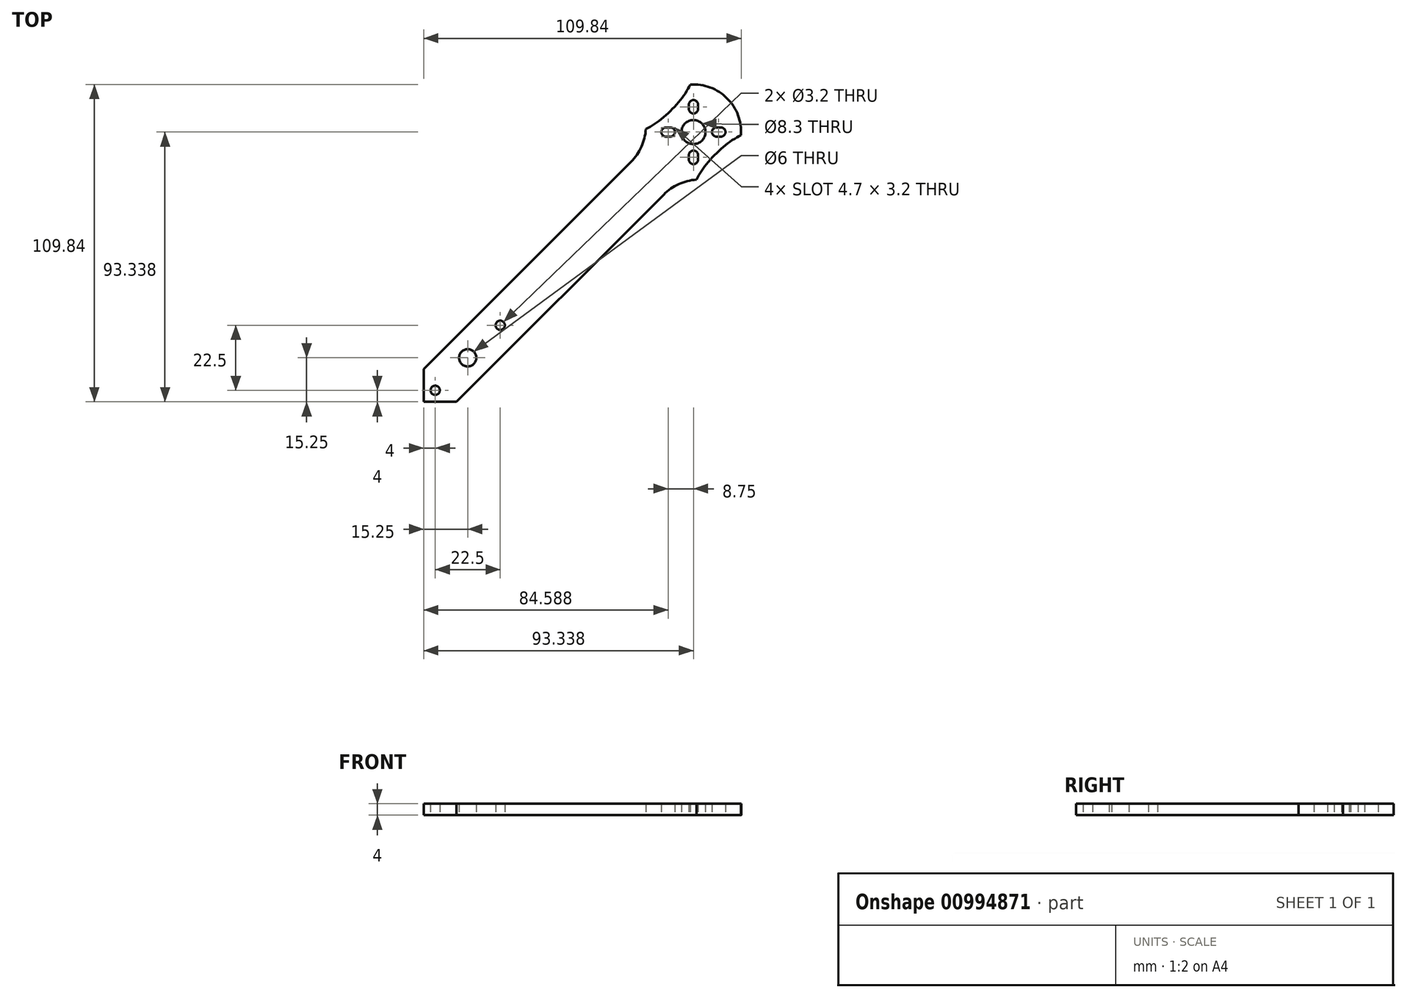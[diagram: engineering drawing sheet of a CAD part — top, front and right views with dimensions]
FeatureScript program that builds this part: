
annotation { "Feature Type Name" : "Feature", "Feature Type Description" : "" }
export const myFeature = defineFeature(function(context is Context, id is Id, definition is map)
    precondition{}
    {
        {
            var Q0;
            Q0=qCreatedBy(makeId("Top.planeOp"),FACE);
            var sketch = newSketch(context, id + "F0", { "sketchPlane" : qUnion([Q0])});
            skLineSegment(sketch, "E0.bottom", {"start": v(-18, 50) * mm, "end": v(18, 50) * mm, "construction": true});
            skLineSegment(sketch, "E0.top", {"start": v(-18, -50) * mm, "end": v(18, -50) * mm, "construction": true});
            skLineSegment(sketch, "E0.left", {"start": v(-18, 50) * mm, "end": v(-18, -50) * mm, "construction": true});
            skLineSegment(sketch, "E0.right", {"start": v(18, 50) * mm, "end": v(18, -50) * mm, "construction": true});
            skPoint(sketch, "E0.middle", {"position": v(0, 0) * mm});
            skLineSegment(sketch, "E1", {"start": v(0, 0) * mm, "end": v(15.25, 0) * mm, "construction": true});
            skLineSegment(sketch, "E2", {"start": v(15.25, 0) * mm, "end": v(15.25, 15.25) * mm, "construction": true});
            skCircle(sketch, "E3", {"center": v(15.25, 15.25) * mm, "radius": 3 * mm});
            skCircle(sketch, "E4.MirrorC", {"center": v(15.25, -15.25) * mm, "radius": 3 * mm, "construction": true});
            skCircle(sketch, "E5.MirrorC", {"center": v(-15.25, -15.25) * mm, "radius": 3 * mm, "construction": true});
            skCircle(sketch, "E6.MirrorC", {"center": v(-15.25, 15.25) * mm, "radius": 3 * mm, "construction": true});
            skLineSegment(sketch, "E7", {"start": v(0, 0) * mm, "end": v(93.34, 93.34) * mm, "construction": true});
            skLineSegment(sketch, "E8", {"start": v(93.34, 93.34) * mm, "end": v(87.68, 99) * mm});
            skLineSegment(sketch, "E9", {"start": v(87.68, 99) * mm, "end": v(99, 87.68) * mm});
            skLineSegment(sketch, "E10", {"start": v(99, 87.68) * mm, "end": v(11.31, 0) * mm});
            skLineSegment(sketch, "E11", {"start": v(11.31, 0) * mm, "end": v(0, 0) * mm});
            skLineSegment(sketch, "E12", {"start": v(87.68, 99) * mm, "end": v(0, 11.31) * mm});
            skLineSegment(sketch, "E13", {"start": v(0, 11.31) * mm, "end": v(0, 0) * mm});
            skCircle(sketch, "E14", {"center": v(93.34, 93.34) * mm, "radius": 16.5 * mm});
            skLineSegment(sketch, "E15", {"start": v(0, 0) * mm, "end": v(4, 0) * mm, "construction": true});
            skLineSegment(sketch, "E16", {"start": v(4, 0) * mm, "end": v(4, 4) * mm, "construction": true});
            skLineSegment(sketch, "E17", {"start": v(4, 4) * mm, "end": v(0, 4) * mm, "construction": true});
            skCircle(sketch, "E18", {"center": v(4, 4) * mm, "radius": 1.6 * mm});
            skLineSegment(sketch, "E19", {"start": v(93.34, 93.34) * mm, "end": v(100.06, 86.62) * mm, "construction": true});
            skCircle(sketch, "E20", {"center": v(100.06, 86.62) * mm, "radius": 1.6 * mm, "construction": true});
            skCircle(sketch, "E21", {"center": v(99, 87.68) * mm, "radius": 1.6 * mm, "construction": true});
            skLineSegment(sketch, "E22", {"start": v(101.19, 87.75) * mm, "end": v(100.13, 88.81) * mm, "construction": true});
            skLineSegment(sketch, "E23", {"start": v(98.93, 85.48) * mm, "end": v(97.86, 86.56) * mm, "construction": true});
            skLineSegment(sketch, "E24", {"start": v(93.34, 93.34) * mm, "end": v(97.6, 91.57) * mm, "construction": true});
            skLineSegment(sketch, "E25", {"start": v(93.34, 93.34) * mm, "end": v(93.34, 77.05) * mm, "construction": true});
            skCircle(sketch, "E26", {"center": v(93.34, 93.34) * mm, "radius": 4.15 * mm});
            skLineSegment(sketch, "E27.MirrorCS", {"start": v(102.84, 91.74) * mm, "end": v(101.34, 91.74) * mm});
            skCircle(sketch, "E28.MirrorC", {"center": v(101.34, 93.34) * mm, "radius": 1.6 * mm});
            skCircle(sketch, "E29.MirrorC", {"center": v(102.84, 93.34) * mm, "radius": 1.6 * mm});
            skLineSegment(sketch, "E30.MirrorCS", {"start": v(94.94, 83.84) * mm, "end": v(94.94, 85.34) * mm});
            skCircle(sketch, "E31.MirrorC", {"center": v(93.34, 83.84) * mm, "radius": 1.6 * mm});
            skCircle(sketch, "E32.MirrorC", {"center": v(93.34, 85.34) * mm, "radius": 1.6 * mm});
            skLineSegment(sketch, "E33.MirrorCS", {"start": v(91.74, 102.84) * mm, "end": v(91.74, 101.34) * mm});
            skCircle(sketch, "E34.MirrorC", {"center": v(93.34, 101.34) * mm, "radius": 1.6 * mm});
            skCircle(sketch, "E35.MirrorC", {"center": v(93.34, 102.84) * mm, "radius": 1.6 * mm});
            skCircle(sketch, "E36.MirrorC", {"center": v(85.34, 93.34) * mm, "radius": 1.6 * mm});
            skCircle(sketch, "E37.MirrorC", {"center": v(83.84, 93.34) * mm, "radius": 1.6 * mm});
            skLineSegment(sketch, "E38.MirrorCS", {"start": v(83.84, 94.94) * mm, "end": v(85.34, 94.94) * mm});
            skLineSegment(sketch, "E39", {"start": v(90.12, 93.34) * mm, "end": v(93.34, 93.34) * mm, "construction": true});
            skLineSegment(sketch, "E40", {"start": v(102.84, 93.34) * mm, "end": v(102.84, 94.94) * mm, "construction": true});
            skLineSegment(sketch, "E41", {"start": v(101.34, 93.34) * mm, "end": v(101.34, 94.94) * mm, "construction": true});
            skLineSegment(sketch, "E42", {"start": v(101.34, 94.94) * mm, "end": v(102.84, 94.94) * mm});
            skLineSegment(sketch, "E43.MirrorCS", {"start": v(93.34, 96.54) * mm, "end": v(100.06, 103.26) * mm, "construction": true});
            skLineSegment(sketch, "E44.MirrorCS", {"start": v(91.74, 85.34) * mm, "end": v(91.74, 83.84) * mm});
            skLineSegment(sketch, "E45.MirrorCS", {"start": v(85.34, 91.74) * mm, "end": v(83.84, 91.74) * mm});
            skLineSegment(sketch, "E46.MirrorCS", {"start": v(94.94, 101.34) * mm, "end": v(94.94, 102.84) * mm});
            skLineSegment(sketch, "E47", {"start": v(89.05, 97.63) * mm, "end": v(81.67, 105) * mm, "construction": true});
            skLineSegment(sketch, "E48", {"start": v(81.67, 105) * mm, "end": v(70.6, 93.93) * mm, "construction": true});
            skEllipse(sketch, "E49", {"center": v(81.67, 105) * mm, "majorRadius": 15.66 * mm, "minorRadius": 5.72 * mm, "majorAxis": v(-0.7, -0.7)});
            skEllipse(sketch, "E50.MirrorC", {"center": v(105, 81.67) * mm, "majorRadius": 15.66 * mm, "minorRadius": 5.72 * mm, "majorAxis": v(-0.7, -0.7)});
            skCircle(sketch, "E51", {"center": v(93.34, 93.34) * mm, "radius": 77.5 * mm, "construction": true});
            skCircle(sketch, "E52", {"center": v(26.5, 26.5) * mm, "radius": 1.6 * mm});
            skSolve(sketch);
        }
        {
            var Q0;
            Q0=makeQuery(id+"F0.imprint","IMPRINT",FACE,{"disambiguationData":[TD([[makeQuery(id+"F0.imprint","IMPRINT",EDGE,{"derivedFrom":sQuery(id+"F0.wireOp",EDGE,"E3")}),-1.0]])]});
            var Q1;
            {var subQ0=sQuery(id+"F0.wireOp",EDGE,"E30.MirrorCS");Q1=makeQuery(id+"F0.imprint","IMPRINT",FACE,{"disambiguationData":[TD([[makeQuery(id+"F0.imprint","IMPRINT",EDGE,{"derivedFrom":subQ0}),-1.0]])]});}
            var Q2;
            {var subQ18=sQuery(id+"F0.wireOp",EDGE,"E27.MirrorCS");Q2=makeQuery(id+"F0.imprint","IMPRINT",FACE,{"disambiguationData":[TD([[makeQuery(id+"F0.imprint","IMPRINT",EDGE,{"derivedFrom":subQ18}),1.0]])]});}
            extrude(context, id + "F1", {"entities" : qUnion([Q0, Q1, Q2]), "depth" : 4 * mm, "offsetDistance" : 25 * mm});
        }
        {
            var Q0;
            Q0=makeQuery(id+"F1.opExtrude","SWEPT_EDGE",EDGE,{"disambiguationData":[OSD([sQuery(id+"F0.wireOp",EDGE,"E10"),sQuery(id+"F0.wireOp",EDGE,"E14")])]});
            var Q1;
            Q1=makeQuery(id+"F1.opExtrude","SWEPT_EDGE",EDGE,{"disambiguationData":[OSD([sQuery(id+"F0.wireOp",EDGE,"E12"),sQuery(id+"F0.wireOp",EDGE,"E14")])]});
            fillet(context, id + "F2", {"entities" : qUnion([Q0, Q1]), "radius" : 17.7 * mm, "tangentPropagation" : true, "defaultsChanged" : true, "vertexSettings" : [], "allowEdgeOverflow" : false});
        }
    });
